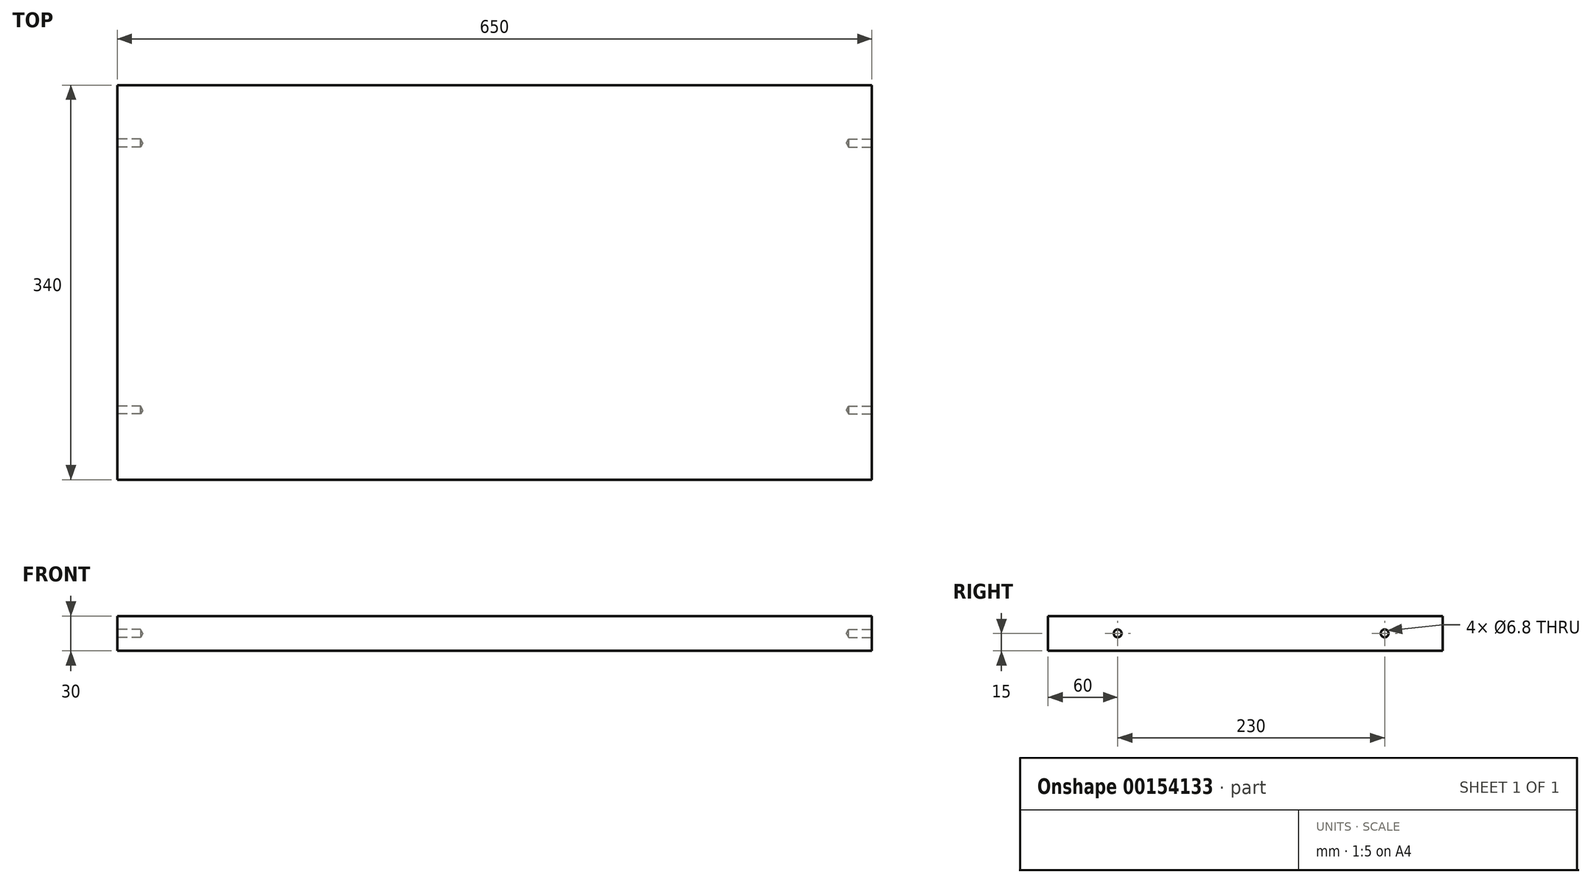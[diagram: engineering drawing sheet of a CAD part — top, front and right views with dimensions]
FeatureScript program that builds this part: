
annotation { "Feature Type Name" : "Feature", "Feature Type Description" : "" }
export const myFeature = defineFeature(function(context is Context, id is Id, definition is map)
    precondition{}
    {
        {
            var Q0;
            Q0=qCreatedBy(makeId("Top.planeOp"),FACE);
            var sketch = newSketch(context, id + "F0", { "sketchPlane" : qUnion([Q0])});
            skLineSegment(sketch, "E0.bottom", {"start": v(325, -170) * mm, "end": v(-325, -170) * mm});
            skLineSegment(sketch, "E0.top", {"start": v(325, 170) * mm, "end": v(-325, 170) * mm});
            skLineSegment(sketch, "E0.left", {"start": v(325, -170) * mm, "end": v(325, 170) * mm});
            skLineSegment(sketch, "E0.right", {"start": v(-325, -170) * mm, "end": v(-325, 170) * mm});
            skPoint(sketch, "E0.middle", {"position": v(0, 0) * mm});
            skSolve(sketch);
        }
        {
            var Q0;
            Q0=qSketchRegion(id+"F0",true);
            extrude(context, id + "F1", {"entities" : qUnion([Q0]), "depth" : 30 * mm});
        }
        {
            var Q0;
            Q0=makeQuery(id+"F1.opExtrude","SWEPT_FACE",FACE,{"disambiguationData":[OSD([sQuery(id+"F0.wireOp",EDGE,"E0.left")])]});
            var sketch = newSketch(context, id + "F2", { "sketchPlane" : qUnion([Q0])});
            skLineSegment(sketch, "E1.bottom", {"start": v(-170, 0) * mm, "end": v(170, 0) * mm});
            skLineSegment(sketch, "E1.top", {"start": v(-170, 30) * mm, "end": v(170, 30) * mm});
            skLineSegment(sketch, "E1.left", {"start": v(-170, 0) * mm, "end": v(-170, 30) * mm});
            skLineSegment(sketch, "E1.right", {"start": v(170, 0) * mm, "end": v(170, 30) * mm});
            skPoint(sketch, "E2", {"position": v(-110, 15) * mm});
            skPoint(sketch, "E3", {"position": v(120, 15) * mm});
            skSolve(sketch);
        }
        {
            var Q0;
            Q0=makeQuery(id+"F1.opExtrude","SWEPT_FACE",FACE,{"disambiguationData":[OSD([sQuery(id+"F0.wireOp",EDGE,"E0.right")])]});
            var sketch = newSketch(context, id + "F3", { "sketchPlane" : qUnion([Q0])});
            skLineSegment(sketch, "E4.bottom", {"start": v(-170, 0) * mm, "end": v(170, 0) * mm});
            skLineSegment(sketch, "E4.top", {"start": v(-170, 30) * mm, "end": v(170, 30) * mm});
            skLineSegment(sketch, "E4.left", {"start": v(-170, 0) * mm, "end": v(-170, 30) * mm});
            skLineSegment(sketch, "E4.right", {"start": v(170, 0) * mm, "end": v(170, 30) * mm});
            skPoint(sketch, "E5", {"position": v(-120, 15) * mm});
            skPoint(sketch, "E6", {"position": v(110, 15) * mm});
            skSolve(sketch);
        }
        {
            var Q0;
            Q0=sQuery(id+"F2.wireOp",VERTEX,"E2");
            var Q1;
            Q1=sQuery(id+"F2.wireOp",VERTEX,"E3");
            var Q2;
            Q2=sQuery(id+"F3.wireOp",VERTEX,"E5");
            var Q3;
            Q3=sQuery(id+"F3.wireOp",VERTEX,"E6");
            var Q4;
            Q4=makeQuery(id+"F1.opExtrude","SWEPT_BODY",BODY,{"disambiguationData":[OSD([sQuery(id+"F0.wireOp",EDGE,"E0.bottom"),sQuery(id+"F0.wireOp",EDGE,"E0.top"),sQuery(id+"F0.wireOp",EDGE,"E0.left"),sQuery(id+"F0.wireOp",EDGE,"E0.right")])]});
            hole(context, id + "F4", {"style" : HoleStyle.SIMPLE, "endStyle" : HoleEndStyle.BLIND, "standardTappedOrClearance" : lookupTablePath({ "standard" : "ISO", "engagement" : "75%", "pitch" : "1.25 mm", "size" : "M8", "type" : "Tapped" }), "standardBlindInLast" : lookupTablePath({ "standard" : "ISO", "engagement" : "75%", "pitch" : "1.25 mm", "size" : "M8", "type" : "Tapped" }), "holeDiameter" : 6.8 * mm, "holeDepth" : 20 * mm, "locations" : qUnion([Q0, Q1, Q2, Q3]), "scope" : qUnion([Q4]), "majorDiameter" : 8 * mm});
        }
    });
